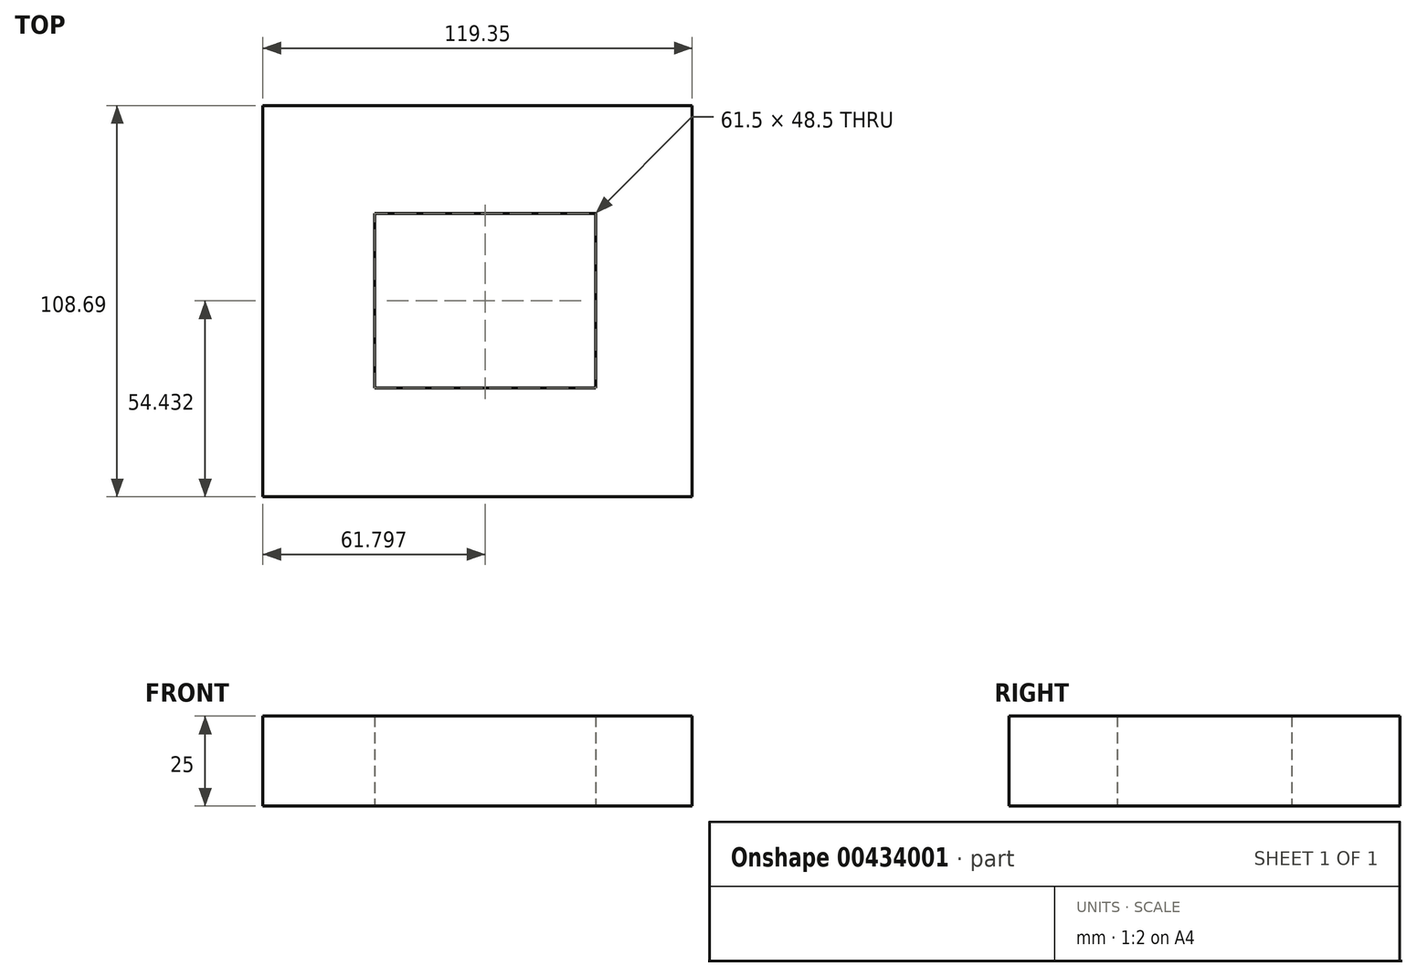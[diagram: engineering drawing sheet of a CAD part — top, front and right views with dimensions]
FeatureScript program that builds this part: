
annotation { "Feature Type Name" : "Feature", "Feature Type Description" : "" }
export const myFeature = defineFeature(function(context is Context, id is Id, definition is map)
    precondition{}
    {
        {
            var Q0;
            Q0=qCreatedBy(makeId("Top.planeOp"),FACE);
            var sketch = newSketch(context, id + "F0", { "sketchPlane" : qUnion([Q0])});
            skLineSegment(sketch, "E0.bottom", {"start": v(-53.14, 50.28) * mm, "end": v(66.2, 50.28) * mm});
            skLineSegment(sketch, "E0.top", {"start": v(-53.14, -58.4) * mm, "end": v(66.2, -58.4) * mm});
            skLineSegment(sketch, "E0.left", {"start": v(-53.14, 50.28) * mm, "end": v(-53.14, -58.4) * mm});
            skLineSegment(sketch, "E0.right", {"start": v(66.2, 50.28) * mm, "end": v(66.2, -58.4) * mm});
            skLineSegment(sketch, "E1.bottom", {"start": v(-22.1, 20.27) * mm, "end": v(39.4, 20.27) * mm});
            skLineSegment(sketch, "E1.top", {"start": v(-22.1, -28.23) * mm, "end": v(39.4, -28.23) * mm});
            skLineSegment(sketch, "E1.left", {"start": v(-22.1, 20.27) * mm, "end": v(-22.1, -28.23) * mm});
            skLineSegment(sketch, "E1.right", {"start": v(39.4, 20.27) * mm, "end": v(39.4, -28.23) * mm});
            skSolve(sketch);
        }
        {
            var Q0;
            Q0=makeQuery(id+"F0.imprint","IMPRINT",FACE,{"disambiguationData":[TD([[makeQuery(id+"F0.imprint","IMPRINT",EDGE,{"derivedFrom":sQuery(id+"F0.wireOp",EDGE,"E0.bottom")}),-1.0]])]});
            extrude(context, id + "F1", {"entities" : qUnion([Q0]), "depth" : 25 * mm});
        }
    });
